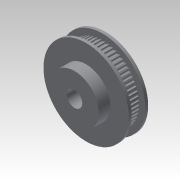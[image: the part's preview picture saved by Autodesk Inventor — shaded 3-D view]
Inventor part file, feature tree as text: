
AUTODESK INVENTOR PART (.ipt)
format: ipt  version: 2022 (Build 260153000, 153)  size: 244,736 bytes
history: native  units: mm
features: sketch x2, revolve x1, extrude x1, pattern_circular x1
ambient origin geometry x8: Origin, YZ Plane, XZ Plane, XY Plane, X Axis, Y Axis, Z Axis, Center Point
bodies: Solid1 (feature_tree)
feature tree (5):
  revolve  "Revolution1"  [1 undecoded]
  extrude  "Extrusion1"  Depth=18.95mm
  pattern_circular  "Circular Pattern1"  Angle=90.0deg  [1 undecoded]
  sketch  "Sketch1"  dims[d0=4.0mm d1=7.0mm]
  sketch  "Sketch2"  dims[d4=1.5mm d6=18.95mm d7=90.0deg d8=1.3mm d9=18.85mm d10=10.0mm d11=0.0mm d12=600.0mm d13=360.0deg d15=22.0mm d16=6.0mm d17=12.5mm]
note: 2 required parameter values undecoded (feature->parameter linkage not recoverable at this tier; creation-order binding heuristic only, values carry confidence <= 0.55)